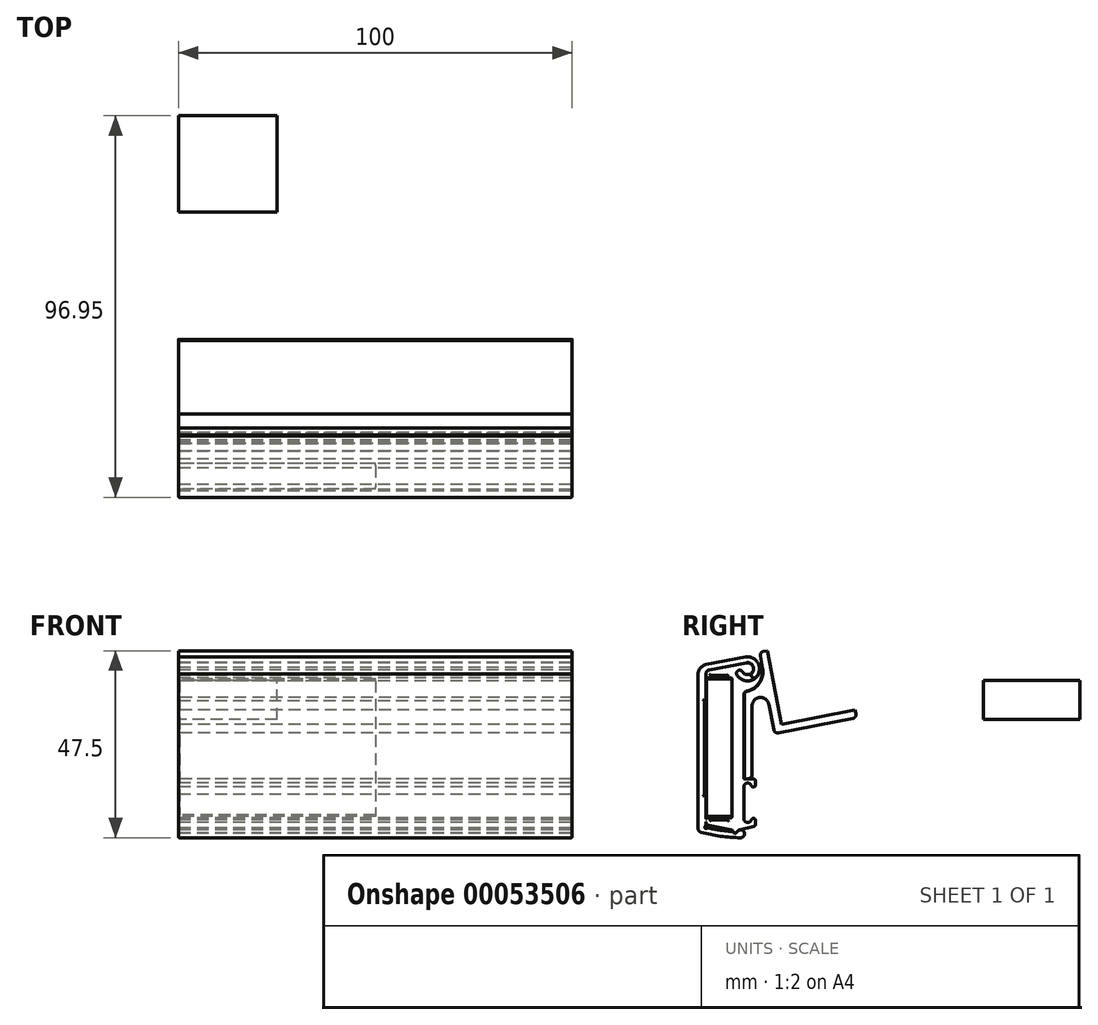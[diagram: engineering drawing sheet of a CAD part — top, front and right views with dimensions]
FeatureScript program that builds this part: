
annotation { "Feature Type Name" : "Feature", "Feature Type Description" : "" }
export const myFeature = defineFeature(function(context is Context, id is Id, definition is map)
    precondition{}
    {
        {
            var Q0;
            Q0=qCreatedBy(makeId("Right.planeOp"),FACE);
            var sketch = newSketch(context, id + "F0", { "sketchPlane" : qUnion([Q0])});
            skLineSegment(sketch, "E0.bottom", {"start": v(-0.5, 35) * mm, "end": v(-6, 35) * mm});
            skLineSegment(sketch, "E0.top", {"start": v(-0.5, 0) * mm, "end": v(-6, 0) * mm});
            skLineSegment(sketch, "E0.left", {"start": v(0, 34.5) * mm, "end": v(0, 0.5) * mm});
            skLineSegment(sketch, "E0.right", {"start": v(-6.5, 34.5) * mm, "end": v(-6.5, 0.5) * mm});
            skPoint(sketch, "E1.visualSharp", {"position": v(0, 35) * mm});
            skArc(sketch, "E1.filletArc", {"start": v(0, 34.5) * mm, "mid": v(-0.15, 34.85) * mm, "end": v(-0.5, 35) * mm});
            skPoint(sketch, "E2.visualSharp", {"position": v(-6.5, 35) * mm});
            skArc(sketch, "E2.filletArc", {"start": v(-6, 35) * mm, "mid": v(-6.35, 34.85) * mm, "end": v(-6.5, 34.5) * mm});
            skPoint(sketch, "E3.visualSharp", {"position": v(-6.5, 0) * mm});
            skArc(sketch, "E3.filletArc", {"start": v(-6.5, 0.5) * mm, "mid": v(-6.35, 0.15) * mm, "end": v(-6, 0) * mm});
            skPoint(sketch, "E4.visualSharp", {"position": v(0, 0) * mm});
            skArc(sketch, "E4.filletArc", {"start": v(-0.5, 0) * mm, "mid": v(-0.15, 0.15) * mm, "end": v(0, 0.5) * mm});
            skLineSegment(sketch, "E5", {"start": v(-6.5, 17.5) * mm, "end": v(0, 17.5) * mm, "construction": true});
            skLineSegment(sketch, "E6.rect.bottom", {"start": v(-3.25, 35.5) * mm, "end": v(-3.25, 35.5) * mm});
            skLineSegment(sketch, "E6.rect.top", {"start": v(-2.25, 34.5) * mm, "end": v(-4.25, 34.5) * mm, "construction": true});
            skLineSegment(sketch, "E6.rect.left", {"start": v(-2.25, 34.5) * mm, "end": v(-2.25, 34.5) * mm});
            skLineSegment(sketch, "E6.rect.right", {"start": v(-4.25, 34.5) * mm, "end": v(-4.25, 34.5) * mm});
            skPoint(sketch, "E6.rect.middle", {"position": v(-3.25, 35) * mm});
            skPoint(sketch, "E7.visualSharp", {"position": v(-4.25, 35.5) * mm});
            skArc(sketch, "E7.filletArc", {"start": v(-3.25, 35.5) * mm, "mid": v(-3.96, 35.2) * mm, "end": v(-4.25, 34.5) * mm, "construction": true});
            skPoint(sketch, "E8.visualSharp", {"position": v(-2.25, 35.5) * mm});
            skArc(sketch, "E8.filletArc", {"start": v(-2.25, 34.5) * mm, "mid": v(-2.54, 35.2) * mm, "end": v(-3.25, 35.5) * mm, "construction": true});
            skPoint(sketch, "E9.MirrorP", {"position": v(-3.25, 0) * mm});
            skPoint(sketch, "E10.MirrorP", {"position": v(-2.25, -0.5) * mm});
            skArc(sketch, "E11.MirrorCS", {"start": v(-2.25, 0.5) * mm, "mid": v(-2.54, -0.2) * mm, "end": v(-3.25, -0.5) * mm, "construction": true});
            skPoint(sketch, "E12.MirrorP", {"position": v(-4.25, -0.5) * mm});
            skLineSegment(sketch, "E13.MirrorCS", {"start": v(-3.25, -0.5) * mm, "end": v(-3.25, -0.5) * mm});
            skArc(sketch, "E14.MirrorCS", {"start": v(-3.25, -0.5) * mm, "mid": v(-3.96, -0.2) * mm, "end": v(-4.25, 0.5) * mm, "construction": true});
            skLineSegment(sketch, "E15.MirrorCS", {"start": v(-4.25, 0.5) * mm, "end": v(-4.25, 0.5) * mm});
            skLineSegment(sketch, "E16.MirrorCS", {"start": v(-2.25, 0.5) * mm, "end": v(-4.25, 0.5) * mm, "construction": true});
            skLineSegment(sketch, "E17.MirrorCS", {"start": v(-2.25, 0.5) * mm, "end": v(-2.25, 0.5) * mm});
            skLineSegment(sketch, "E18.rect.bottom", {"start": v(-6, 29.4) * mm, "end": v(-6.5, 29.4) * mm});
            skLineSegment(sketch, "E18.rect.top", {"start": v(-6, 5.6) * mm, "end": v(-6.5, 5.6) * mm});
            skLineSegment(sketch, "E18.rect.left", {"start": v(-6, 29.4) * mm, "end": v(-6, 5.6) * mm, "construction": true});
            skPoint(sketch, "E18.rect.middle", {"position": v(-6.5, 17.5) * mm});
            skPoint(sketch, "E18.rect.right.end.orphan", {"position": v(-7, 5.6) * mm});
            skPoint(sketch, "E18.rect.right.start.orphan", {"position": v(-7, 29.4) * mm});
            skSolve(sketch);
        }
        {
            var Q0;
            Q0=qCreatedBy(makeId("Right.planeOp"),FACE);
            var sketch = newSketch(context, id + "F1", { "sketchPlane" : qUnion([Q0])});
            skLineSegment(sketch, "E19", {"start": v(-6.3, 35.3) * mm, "end": v(-5.65, 35.3) * mm});
            skLineSegment(sketch, "E20", {"start": v(0, 35) * mm, "end": v(0, 0) * mm});
            skLineSegment(sketch, "E21", {"start": v(-0.3, -0.3) * mm, "end": v(-0.85, -0.3) * mm});
            skLineSegment(sketch, "E22", {"start": v(-12.05, -2.3) * mm, "end": v(-5.6, -2.3) * mm, "construction": true});
            skLineSegment(sketch, "E23", {"start": v(-5.35, 35.6) * mm, "end": v(-5.35, 35.85) * mm});
            skLineSegment(sketch, "E24", {"start": v(-5.35, 35.85) * mm, "end": v(-1.15, 35.85) * mm});
            skLineSegment(sketch, "E25", {"start": v(-1.15, 35.85) * mm, "end": v(-1.15, 35.6) * mm});
            skLineSegment(sketch, "E26.trimOffspring", {"start": v(-0.85, 35.3) * mm, "end": v(-0.3, 35.3) * mm});
            skLineSegment(sketch, "E27.MirrorCS", {"start": v(-1.15, -0.85) * mm, "end": v(-1.15, -0.6) * mm});
            skLineSegment(sketch, "E28.MirrorCS", {"start": v(-5.35, -0.6) * mm, "end": v(-5.35, -0.85) * mm});
            skLineSegment(sketch, "E29.MirrorCS", {"start": v(-5.35, -0.85) * mm, "end": v(-1.15, -0.85) * mm});
            skLineSegment(sketch, "E30.trimOffspring", {"start": v(-5.65, -0.3) * mm, "end": v(-6.3, -0.3) * mm});
            skPoint(sketch, "E31.visualSharp", {"position": v(-6, 35.3) * mm});
            skArc(sketch, "E31.filletArc", {"start": v(-6.6, 35.6) * mm, "mid": v(-6.51, 35.39) * mm, "end": v(-6.3, 35.3) * mm});
            skPoint(sketch, "E32.visualSharp", {"position": v(-5.35, 35.3) * mm});
            skArc(sketch, "E32.filletArc", {"start": v(-5.65, 35.3) * mm, "mid": v(-5.44, 35.39) * mm, "end": v(-5.35, 35.6) * mm});
            skPoint(sketch, "E33.visualSharp", {"position": v(0, 35.3) * mm});
            skArc(sketch, "E33.filletArc", {"start": v(0, 35) * mm, "mid": v(-0.09, 35.21) * mm, "end": v(-0.3, 35.3) * mm});
            skPoint(sketch, "E34.visualSharp", {"position": v(-1.15, 35.3) * mm});
            skArc(sketch, "E34.filletArc", {"start": v(-1.15, 35.6) * mm, "mid": v(-1.06, 35.39) * mm, "end": v(-0.85, 35.3) * mm});
            skPoint(sketch, "E35.visualSharp", {"position": v(-6, -0.3) * mm});
            skArc(sketch, "E35.filletArc", {"start": v(-6.3, -0.3) * mm, "mid": v(-6.51, -0.39) * mm, "end": v(-6.6, -0.6) * mm});
            skPoint(sketch, "E36.visualSharp", {"position": v(-5.35, -0.3) * mm});
            skArc(sketch, "E36.filletArc", {"start": v(-5.35, -0.6) * mm, "mid": v(-5.44, -0.39) * mm, "end": v(-5.65, -0.3) * mm});
            skPoint(sketch, "E37.visualSharp", {"position": v(-1.15, -0.3) * mm});
            skArc(sketch, "E37.filletArc", {"start": v(-0.85, -0.3) * mm, "mid": v(-1.06, -0.39) * mm, "end": v(-1.15, -0.6) * mm});
            skPoint(sketch, "E38.visualSharp", {"position": v(0, -0.3) * mm});
            skArc(sketch, "E38.filletArc", {"start": v(-0.3, -0.3) * mm, "mid": v(-0.09, -0.21) * mm, "end": v(0, 0) * mm});
            skPoint(sketch, "E39.visualSharp", {"position": v(1.45, 37.5) * mm});
            skPoint(sketch, "E40.visualSharp", {"position": v(-6, 37.5) * mm});
            skPoint(sketch, "E41.visualSharp", {"position": v(-6, -2.3) * mm});
            skArc(sketch, "E41.filletArc", {"start": v(-6.6, -1.3) * mm, "mid": v(-6.37, -1.94) * mm, "end": v(-5.79, -2.28) * mm});
            skArc(sketch, "E42", {"start": v(4.02, -3.35) * mm, "mid": v(-6.17, -2.3) * mm, "end": v(-15.75, 1.34) * mm, "construction": true});
            skLineSegment(sketch, "E43", {"start": v(-5.79, -2.28) * mm, "end": v(-0.09, -3.38) * mm});
            skArc(sketch, "E44", {"start": v(0.23, -3.7) * mm, "mid": v(0.7, -4.17) * mm, "end": v(1.31, -3.87) * mm});
            skPoint(sketch, "E45.visualSharp", {"position": v(0.24, -3.44) * mm});
            skArc(sketch, "E45.filletArc", {"start": v(0.23, -3.7) * mm, "mid": v(0.12, -3.49) * mm, "end": v(-0.09, -3.38) * mm});
            skPoint(sketch, "E46.visualSharp", {"position": v(1.32, -3.33) * mm});
            skPoint(sketch, "E47.visualSharp", {"position": v(-12.05, -2.3) * mm});
            skLineSegment(sketch, "E48", {"start": v(5.5, 9.53) * mm, "end": v(3.23, 9.53) * mm});
            skPoint(sketch, "E49.visualSharp", {"position": v(7.02, 9.53) * mm});
            skLineSegment(sketch, "E50.trimOffspring", {"start": v(3.03, 9.73) * mm, "end": v(3.03, 30.94) * mm});
            skPoint(sketch, "E51.visualSharp", {"position": v(7.02, 6.35) * mm});
            skPoint(sketch, "E52.visualSharp", {"position": v(3.03, 9.53) * mm});
            skArc(sketch, "E52.filletArc", {"start": v(3.03, 9.73) * mm, "mid": v(3.1, 9.6) * mm, "end": v(3.23, 9.53) * mm});
            skLineSegment(sketch, "E53", {"start": v(6, 9.03) * mm, "end": v(6, 8.03) * mm});
            skLineSegment(sketch, "E54", {"start": v(5.5, 7.53) * mm, "end": v(5.41, 7.53) * mm});
            skLineSegment(sketch, "E55", {"start": v(3, 7.53) * mm, "end": v(3, -0.47) * mm});
            skLineSegment(sketch, "E56", {"start": v(5.41, -0.47) * mm, "end": v(5.5, -0.47) * mm});
            skArc(sketch, "E57", {"start": v(3, 7.53) * mm, "mid": v(3.83, 8.51) * mm, "end": v(4.94, 7.86) * mm});
            skArc(sketch, "E58", {"start": v(3, -0.47) * mm, "mid": v(3.83, -1.46) * mm, "end": v(4.94, -0.8) * mm});
            skPoint(sketch, "E59.visualSharp", {"position": v(5, 7.53) * mm});
            skArc(sketch, "E59.filletArc", {"start": v(4.94, 7.86) * mm, "mid": v(5.13, 7.62) * mm, "end": v(5.41, 7.53) * mm});
            skPoint(sketch, "E60.newPointA", {"position": v(7, 7.53) * mm});
            skArc(sketch, "E60.filletArc", {"start": v(5.5, 7.53) * mm, "mid": v(5.85, 7.67) * mm, "end": v(6, 8.03) * mm});
            skPoint(sketch, "E61.visualSharp", {"position": v(5, -0.47) * mm});
            skArc(sketch, "E61.filletArc", {"start": v(5.41, -0.47) * mm, "mid": v(5.13, -0.57) * mm, "end": v(4.94, -0.8) * mm});
            skLineSegment(sketch, "E62", {"start": v(6, -0.97) * mm, "end": v(6, -1.98) * mm});
            skPoint(sketch, "E63.visualSharp", {"position": v(6, -0.47) * mm});
            skArc(sketch, "E63.filletArc", {"start": v(6, -0.97) * mm, "mid": v(5.85, -0.62) * mm, "end": v(5.5, -0.47) * mm});
            skPoint(sketch, "E64.visualSharp", {"position": v(6, 9.53) * mm});
            skArc(sketch, "E64.filletArc", {"start": v(6, 9.03) * mm, "mid": v(5.85, 9.39) * mm, "end": v(5.5, 9.53) * mm});
            skLineSegment(sketch, "E65.bottom", {"start": v(-5.35, 35.85) * mm, "end": v(-1.15, 35.85) * mm, "construction": true});
            skLineSegment(sketch, "E65.top", {"start": v(-5.35, 35.5) * mm, "end": v(-1.15, 35.5) * mm, "construction": true});
            skLineSegment(sketch, "E65.left", {"start": v(-5.35, 35.85) * mm, "end": v(-5.35, 35.5) * mm, "construction": true});
            skLineSegment(sketch, "E65.right", {"start": v(-1.15, 35.85) * mm, "end": v(-1.15, 35.5) * mm, "construction": true});
            skLineSegment(sketch, "E66", {"start": v(-3.25, 35.85) * mm, "end": v(-3.25, 34.98) * mm, "construction": true});
            skPoint(sketch, "E66.endSnap0", {"position": v(-3.25, 35.85) * mm});
            skLineSegment(sketch, "E67", {"start": v(-6.6, -0.6) * mm, "end": v(-6.6, -1.3) * mm});
            skPoint(sketch, "E68.startSnap0", {"position": v(5.5, 34.89) * mm});
            skLineSegment(sketch, "E69", {"start": v(3.03, 31.44) * mm, "end": v(3.03, 35.7) * mm, "construction": true});
            skPoint(sketch, "E70.visualSharp", {"position": v(3.03, 30.76) * mm});
            skArc(sketch, "E70.filletArc", {"start": v(4.46, 30.97) * mm, "mid": v(3.43, 30.25) * mm, "end": v(3.03, 29.06) * mm, "construction": true});
            skArc(sketch, "E71", {"start": v(1.31, -3.87) * mm, "mid": v(1.58, -3.56) * mm, "end": v(1.96, -3.38) * mm});
            skLineSegment(sketch, "E72", {"start": v(1.96, -3.38) * mm, "end": v(5.62, -2.47) * mm});
            skPoint(sketch, "E73.visualSharp", {"position": v(6, -2.37) * mm});
            skArc(sketch, "E73.filletArc", {"start": v(5.62, -2.47) * mm, "mid": v(5.9, -2.29) * mm, "end": v(6, -1.98) * mm});
            skArc(sketch, "E74", {"start": v(3.69, 39.04) * mm, "mid": v(5.32, 36.94) * mm, "end": v(2.66, 36.81) * mm});
            skLineSegment(sketch, "E75", {"start": v(-5.73, 37.3) * mm, "end": v(3.69, 39.04) * mm});
            skArc(sketch, "E76", {"start": v(-5.73, 37.3) * mm, "mid": v(-6.35, 36.93) * mm, "end": v(-6.6, 36.25) * mm});
            skLineSegment(sketch, "E77", {"start": v(-6.6, 35.6) * mm, "end": v(-6.6, 36.25) * mm});
            skLineSegment(sketch, "E78", {"start": v(3.96, 37.56) * mm, "end": v(2.66, 36.81) * mm, "construction": true});
            skArc(sketch, "E79", {"start": v(1.28, 36.01) * mm, "mid": v(4.76, 34.57) * mm, "end": v(7.06, 37.56) * mm});
            skArc(sketch, "E80", {"start": v(7.06, 37.56) * mm, "mid": v(7.37, 37.9) * mm, "end": v(7.72, 37.62) * mm});
            skArc(sketch, "E81", {"start": v(7.72, 37.62) * mm, "mid": v(6.91, 33.99) * mm, "end": v(3.83, 31.92) * mm});
            skArc(sketch, "E82", {"start": v(2.66, 36.81) * mm, "mid": v(1.57, 37.1) * mm, "end": v(1.28, 36.01) * mm});
            skPoint(sketch, "E83.visualSharp", {"position": v(3.03, 31.82) * mm});
            skArc(sketch, "E83.filletArc", {"start": v(3.83, 31.92) * mm, "mid": v(3.26, 31.57) * mm, "end": v(3.03, 30.94) * mm});
            skLineSegment(sketch, "E84", {"start": v(3.96, 37.56) * mm, "end": v(7.4, 37.56) * mm, "construction": true});
            skLineSegment(sketch, "E85", {"start": v(3.96, 37.56) * mm, "end": v(3.96, 34.96) * mm, "construction": true});
            skSolve(sketch);
        }
        {
            var Q0;
            Q0=qCreatedBy(makeId("Right.planeOp"),FACE);
            var sketch = newSketch(context, id + "F2", { "sketchPlane" : qUnion([Q0])});
            skLineSegment(sketch, "E86.2", {"start": v(-5.6, 37.3) * mm, "end": v(-5.6, 37.3) * mm});
            skArc(sketch, "E87.1", {"start": v(-6.58, 38.62) * mm, "mid": v(-7.99, 37.8) * mm, "end": v(-8.6, 36.3) * mm});
            skLineSegment(sketch, "E88", {"start": v(-8.6, 36.3) * mm, "end": v(-8.6, -3) * mm});
            skPoint(sketch, "E89.visualSharp", {"position": v(-6.03, 35.1) * mm});
            skArc(sketch, "E90", {"start": v(-5.8, -2.92) * mm, "mid": v(-2.9, -3.45) * mm, "end": v(0.01, -3.77) * mm});
            skArc(sketch, "E91.0", {"start": v(-7.86, -3.96) * mm, "mid": v(-2.88, -4.97) * mm, "end": v(2.18, -5.37) * mm});
            skPoint(sketch, "E92.trimOffspring.end.orphan", {"position": v(-7.6, -5.55) * mm});
            skPoint(sketch, "E93.orphan", {"position": v(-8.6, -5.55) * mm});
            skPoint(sketch, "E94.visualSharp", {"position": v(-8.6, -3.75) * mm});
            skArc(sketch, "E94.filletArc", {"start": v(-8.6, -3) * mm, "mid": v(-8.4, -3.6) * mm, "end": v(-7.86, -3.96) * mm});
            skPoint(sketch, "E95.visualSharp", {"position": v(12.44, -2.73) * mm});
            skLineSegment(sketch, "E96.0", {"start": v(-6.6, 36.25) * mm, "end": v(-6.6, 29.4) * mm});
            skArc(sketch, "E97", {"start": v(-6.83, -2.54) * mm, "mid": v(-6.83, -2.92) * mm, "end": v(-6.46, -3) * mm});
            skPoint(sketch, "E98.visualSharp", {"position": v(-6.6, -2.43) * mm});
            skArc(sketch, "E98.filletArc", {"start": v(-6.83, -2.54) * mm, "mid": v(-6.66, -2.24) * mm, "end": v(-6.6, -1.9) * mm});
            skPoint(sketch, "E99.visualSharp", {"position": v(-6.3, -2.8) * mm});
            skArc(sketch, "E99.filletArc", {"start": v(-5.8, -2.92) * mm, "mid": v(-6.14, -2.9) * mm, "end": v(-6.46, -3) * mm});
            skPoint(sketch, "E100.visualSharp", {"position": v(0.78, -3.82) * mm});
            skLineSegment(sketch, "E101", {"start": v(-6.6, 29.4) * mm, "end": v(-7, 29.4) * mm});
            skLineSegment(sketch, "E102", {"start": v(-6.6, 5.6) * mm, "end": v(-7, 5.6) * mm});
            skLineSegment(sketch, "E103", {"start": v(-7, 5.6) * mm, "end": v(-7, 29.4) * mm});
            skLineSegment(sketch, "E104.trimOffspring", {"start": v(-6.6, 5.6) * mm, "end": v(-6.6, -1.9) * mm});
            skArc(sketch, "E105", {"start": v(1.33, -3.88) * mm, "mid": v(3.07, -3.87) * mm, "end": v(2.18, -5.37) * mm});
            skArc(sketch, "E106", {"start": v(0.31, -3.94) * mm, "mid": v(0.83, -4.2) * mm, "end": v(1.33, -3.88) * mm});
            skPoint(sketch, "E107.visualSharp", {"position": v(0.23, -3.78) * mm});
            skArc(sketch, "E107.filletArc", {"start": v(0.31, -3.94) * mm, "mid": v(0.18, -3.82) * mm, "end": v(0.01, -3.77) * mm});
            skLineSegment(sketch, "E108", {"start": v(-6.58, 38.62) * mm, "end": v(3.39, 40.54) * mm});
            skLineSegment(sketch, "E109", {"start": v(-5.74, 37.3) * mm, "end": v(3.66, 39.1) * mm});
            skArc(sketch, "E110", {"start": v(3.39, 40.54) * mm, "mid": v(6.63, 39) * mm, "end": v(6.14, 35.46) * mm});
            skArc(sketch, "E111", {"start": v(3.66, 39.1) * mm, "mid": v(5.34, 38.31) * mm, "end": v(5.09, 36.47) * mm});
            skLineSegment(sketch, "E112", {"start": v(3.96, 37.56) * mm, "end": v(11, 38.92) * mm, "construction": true});
            skLineSegment(sketch, "E113", {"start": v(3.96, 37.56) * mm, "end": v(6.14, 35.46) * mm, "construction": true});
            skArc(sketch, "E114", {"start": v(5.09, 36.47) * mm, "mid": v(5.1, 35.44) * mm, "end": v(6.14, 35.46) * mm});
            skArc(sketch, "E115", {"start": v(-6.6, 36.25) * mm, "mid": v(-6.36, 36.93) * mm, "end": v(-5.74, 37.3) * mm});
            skSolve(sketch);
        }
        {
            var Q0;
            Q0=qCreatedBy(makeId("Right.planeOp"),FACE);
            var sketch = newSketch(context, id + "F3", { "sketchPlane" : qUnion([Q0])});
            skLineSegment(sketch, "E116.2", {"start": v(3.13, 9.63) * mm, "end": v(3.13, 30.94) * mm});
            skLineSegment(sketch, "E117", {"start": v(3.13, 9.63) * mm, "end": v(4.13, 9.63) * mm});
            skLineSegment(sketch, "E118", {"start": v(5.13, 10.63) * mm, "end": v(5.13, 28.17) * mm});
            skPoint(sketch, "E119.visualSharp", {"position": v(7, 40) * mm});
            skArc(sketch, "E119.filletArc", {"start": v(8.01, 41.94) * mm, "mid": v(7.37, 41.52) * mm, "end": v(7.22, 40.77) * mm});
            skPoint(sketch, "E120.visualSharp", {"position": v(11.58, -2.41) * mm});
            skLineSegment(sketch, "E121", {"start": v(8.01, 41.94) * mm, "end": v(9, 42.13) * mm});
            skLineSegment(sketch, "E122", {"start": v(7.8, 37.78) * mm, "end": v(7.22, 40.77) * mm});
            skLineSegment(sketch, "E123", {"start": v(9, 42.13) * mm, "end": v(12.6, 23.47) * mm});
            skLineSegment(sketch, "E124", {"start": v(12.6, 23.47) * mm, "end": v(31.25, 27.07) * mm});
            skLineSegment(sketch, "E125", {"start": v(31.25, 27.07) * mm, "end": v(31.48, 26.16) * mm});
            skLineSegment(sketch, "E126", {"start": v(30.7, 24.93) * mm, "end": v(11.79, 21.28) * mm});
            skLineSegment(sketch, "E127", {"start": v(10.62, 22.07) * mm, "end": v(9.36, 28.57) * mm});
            skArc(sketch, "E128", {"start": v(9.36, 28.57) * mm, "mid": v(7.06, 30.3) * mm, "end": v(5.13, 28.17) * mm});
            skArc(sketch, "E129.0", {"start": v(3.85, 31.82) * mm, "mid": v(3.33, 31.5) * mm, "end": v(3.13, 30.94) * mm});
            skArc(sketch, "E129.1", {"start": v(7.8, 37.78) * mm, "mid": v(7.04, 34) * mm, "end": v(3.85, 31.82) * mm});
            skPoint(sketch, "E130.visualSharp", {"position": v(10.8, 21.1) * mm});
            skArc(sketch, "E130.filletArc", {"start": v(10.62, 22.07) * mm, "mid": v(11.04, 21.44) * mm, "end": v(11.79, 21.28) * mm});
            skPoint(sketch, "E131.visualSharp", {"position": v(31.75, 25.13) * mm});
            skArc(sketch, "E131.filletArc", {"start": v(30.7, 24.93) * mm, "mid": v(31.36, 25.38) * mm, "end": v(31.48, 26.16) * mm});
            skPoint(sketch, "E132.visualSharp", {"position": v(5.13, 9.63) * mm});
            skArc(sketch, "E132.filletArc", {"start": v(4.13, 9.63) * mm, "mid": v(4.84, 9.93) * mm, "end": v(5.13, 10.63) * mm});
            skSolve(sketch);
        }
        {
            var Q0;
            Q0=qSketchRegion(id+"F1",true);
            extrude(context, id + "F4", {"entities" : qUnion([Q0]), "depth" : 100 * mm});
        }
        {
            var Q0;
            Q0=qSketchRegion(id+"F2",true);
            extrude(context, id + "F5", {"entities" : qUnion([Q0]), "depth" : 100 * mm});
        }
        {
            var Q0;
            Q0=makeQuery(id+"F5.opExtrude","CAP_FACE",FACE,{"disambiguationData":[OSD([sQuery(id+"F2.wireOp",EDGE,"E86.2"),sQuery(id+"F2.wireOp",EDGE,"E86.3"),sQuery(id+"F2.wireOp",EDGE,"E87.1"),sQuery(id+"F2.wireOp",EDGE,"E88"),sQuery(id+"F2.wireOp",EDGE,"E90"),sQuery(id+"F2.wireOp",EDGE,"E91.0"),sQuery(id+"F2.wireOp",EDGE,"E94.filletArc"),sQuery(id+"F2.wireOp",EDGE,"E96.0"),sQuery(id+"F2.wireOp",EDGE,"E97"),sQuery(id+"F2.wireOp",EDGE,"E98.filletArc"),sQuery(id+"F2.wireOp",EDGE,"E99.filletArc"),sQuery(id+"F2.wireOp",EDGE,"E101"),sQuery(id+"F2.wireOp",EDGE,"E102"),sQuery(id+"F2.wireOp",EDGE,"E103"),sQuery(id+"F2.wireOp",EDGE,"E104.trimOffspring"),sQuery(id+"F2.wireOp",EDGE,"a8f8e689-5e16-47e5-8057-b0ad275942a9"),sQuery(id+"F2.wireOp",EDGE,"E105"),sQuery(id+"F2.wireOp",EDGE,"E106"),sQuery(id+"F2.wireOp",EDGE,"E107.filletArc"),sQuery(id+"F2.wireOp",EDGE,"12610329-de8c-4fad-bd06-cedb4965ef3b.0"),sQuery(id+"F2.wireOp",EDGE,"fd023df9-4820-42a8-a1c4-7477257e8a0a.0"),sQuery(id+"F2.wireOp",EDGE,"7f343079-0b22-43a6-ac4e-2e25a93e7ffd")])],"isStart":false});
            var Q1;
            Q1=makeQuery(id+"F5.opExtrude","CAP_FACE",FACE,{"disambiguationData":[OSD([sQuery(id+"F2.wireOp",EDGE,"E86.2"),sQuery(id+"F2.wireOp",EDGE,"E86.3"),sQuery(id+"F2.wireOp",EDGE,"E87.1"),sQuery(id+"F2.wireOp",EDGE,"E88"),sQuery(id+"F2.wireOp",EDGE,"E90"),sQuery(id+"F2.wireOp",EDGE,"E91.0"),sQuery(id+"F2.wireOp",EDGE,"E94.filletArc"),sQuery(id+"F2.wireOp",EDGE,"E96.0"),sQuery(id+"F2.wireOp",EDGE,"E97"),sQuery(id+"F2.wireOp",EDGE,"E98.filletArc"),sQuery(id+"F2.wireOp",EDGE,"E99.filletArc"),sQuery(id+"F2.wireOp",EDGE,"E101"),sQuery(id+"F2.wireOp",EDGE,"E102"),sQuery(id+"F2.wireOp",EDGE,"E103"),sQuery(id+"F2.wireOp",EDGE,"E104.trimOffspring"),sQuery(id+"F2.wireOp",EDGE,"a8f8e689-5e16-47e5-8057-b0ad275942a9"),sQuery(id+"F2.wireOp",EDGE,"E105"),sQuery(id+"F2.wireOp",EDGE,"E106"),sQuery(id+"F2.wireOp",EDGE,"E107.filletArc"),sQuery(id+"F2.wireOp",EDGE,"12610329-de8c-4fad-bd06-cedb4965ef3b.0"),sQuery(id+"F2.wireOp",EDGE,"fd023df9-4820-42a8-a1c4-7477257e8a0a.0"),sQuery(id+"F2.wireOp",EDGE,"7f343079-0b22-43a6-ac4e-2e25a93e7ffd")])],"isStart":true});
            fillet(context, id + "F6", {"entities" : qUnion([Q0, Q1]), "radius" : .3 * mm, "tangentPropagation" : true, "allowEdgeOverflow" : false});
        }
        {
            var Q0;
            Q0=makeQuery(id+"F4.opExtrude","CAP_FACE",FACE,{"disambiguationData":[OSD([sQuery(id+"F1.wireOp",EDGE,"E19"),sQuery(id+"F1.wireOp",EDGE,"E20"),sQuery(id+"F1.wireOp",EDGE,"E21"),sQuery(id+"F1.wireOp",EDGE,"E23"),sQuery(id+"F1.wireOp",EDGE,"E24"),sQuery(id+"F1.wireOp",EDGE,"E25"),sQuery(id+"F1.wireOp",EDGE,"E26.trimOffspring"),sQuery(id+"F1.wireOp",EDGE,"E27.MirrorCS"),sQuery(id+"F1.wireOp",EDGE,"E28.MirrorCS"),sQuery(id+"F1.wireOp",EDGE,"E29.MirrorCS"),sQuery(id+"F1.wireOp",EDGE,"E30.trimOffspring"),sQuery(id+"F1.wireOp",EDGE,"E31.filletArc"),sQuery(id+"F1.wireOp",EDGE,"E32.filletArc"),sQuery(id+"F1.wireOp",EDGE,"E33.filletArc"),sQuery(id+"F1.wireOp",EDGE,"E34.filletArc"),sQuery(id+"F1.wireOp",EDGE,"E35.filletArc"),sQuery(id+"F1.wireOp",EDGE,"E36.filletArc"),sQuery(id+"F1.wireOp",EDGE,"E37.filletArc"),sQuery(id+"F1.wireOp",EDGE,"E38.filletArc"),sQuery(id+"F1.wireOp",EDGE,"E40.filletArc"),sQuery(id+"F1.wireOp",EDGE,"E41.filletArc"),sQuery(id+"F1.wireOp",EDGE,"E43"),sQuery(id+"F1.wireOp",EDGE,"E44"),sQuery(id+"F1.wireOp",EDGE,"E45.filletArc"),sQuery(id+"F1.wireOp",EDGE,"E48"),sQuery(id+"F1.wireOp",EDGE,"E50.trimOffspring"),sQuery(id+"F1.wireOp",EDGE,"E52.filletArc"),sQuery(id+"F1.wireOp",EDGE,"E53"),sQuery(id+"F1.wireOp",EDGE,"E54"),sQuery(id+"F1.wireOp",EDGE,"E55"),sQuery(id+"F1.wireOp",EDGE,"E56"),sQuery(id+"F1.wireOp",EDGE,"E57"),sQuery(id+"F1.wireOp",EDGE,"E58"),sQuery(id+"F1.wireOp",EDGE,"E59.filletArc"),sQuery(id+"F1.wireOp",EDGE,"E60.filletArc"),sQuery(id+"F1.wireOp",EDGE,"E61.filletArc"),sQuery(id+"F1.wireOp",EDGE,"E62"),sQuery(id+"F1.wireOp",EDGE,"E63.filletArc"),sQuery(id+"F1.wireOp",EDGE,"E64.filletArc"),sQuery(id+"F1.wireOp",EDGE,"9542a1ec-a0dd-46c9-bb78-918edde2ff07"),sQuery(id+"F1.wireOp",EDGE,"98c17557-ba8b-4a89-b03a-64bb9ddbf5dd"),sQuery(id+"F1.wireOp",EDGE,"E67"),sQuery(id+"F1.wireOp",EDGE,"bf3c36d9-637c-44d3-a7fd-f6e3cdd292ba"),sQuery(id+"F1.wireOp",EDGE,"c5bfcd06-bca6-4be6-b2b0-0e9924831b46"),sQuery(id+"F1.wireOp",EDGE,"5fbb8a50-3f5f-4460-b2ad-e5d3e9a667ab"),sQuery(id+"F1.wireOp",EDGE,"fa309500-8770-4dd0-bda2-21b0fca20fbb"),sQuery(id+"F1.wireOp",EDGE,"0d5ed8aa-ec24-4a5e-be27-1346574a6d7d"),sQuery(id+"F1.wireOp",EDGE,"E70.filletArc"),sQuery(id+"F1.wireOp",EDGE,"E71"),sQuery(id+"F1.wireOp",EDGE,"E72"),sQuery(id+"F1.wireOp",EDGE,"E73.filletArc")])],"isStart":false});
            var Q1;
            Q1=makeQuery(id+"F4.opExtrude","CAP_FACE",FACE,{"disambiguationData":[OSD([sQuery(id+"F1.wireOp",EDGE,"E19"),sQuery(id+"F1.wireOp",EDGE,"E20"),sQuery(id+"F1.wireOp",EDGE,"E21"),sQuery(id+"F1.wireOp",EDGE,"E23"),sQuery(id+"F1.wireOp",EDGE,"E24"),sQuery(id+"F1.wireOp",EDGE,"E25"),sQuery(id+"F1.wireOp",EDGE,"E26.trimOffspring"),sQuery(id+"F1.wireOp",EDGE,"E27.MirrorCS"),sQuery(id+"F1.wireOp",EDGE,"E28.MirrorCS"),sQuery(id+"F1.wireOp",EDGE,"E29.MirrorCS"),sQuery(id+"F1.wireOp",EDGE,"E30.trimOffspring"),sQuery(id+"F1.wireOp",EDGE,"E31.filletArc"),sQuery(id+"F1.wireOp",EDGE,"E32.filletArc"),sQuery(id+"F1.wireOp",EDGE,"E33.filletArc"),sQuery(id+"F1.wireOp",EDGE,"E34.filletArc"),sQuery(id+"F1.wireOp",EDGE,"E35.filletArc"),sQuery(id+"F1.wireOp",EDGE,"E36.filletArc"),sQuery(id+"F1.wireOp",EDGE,"E37.filletArc"),sQuery(id+"F1.wireOp",EDGE,"E38.filletArc"),sQuery(id+"F1.wireOp",EDGE,"E40.filletArc"),sQuery(id+"F1.wireOp",EDGE,"E41.filletArc"),sQuery(id+"F1.wireOp",EDGE,"E43"),sQuery(id+"F1.wireOp",EDGE,"E44"),sQuery(id+"F1.wireOp",EDGE,"E45.filletArc"),sQuery(id+"F1.wireOp",EDGE,"E48"),sQuery(id+"F1.wireOp",EDGE,"E50.trimOffspring"),sQuery(id+"F1.wireOp",EDGE,"E52.filletArc"),sQuery(id+"F1.wireOp",EDGE,"E53"),sQuery(id+"F1.wireOp",EDGE,"E54"),sQuery(id+"F1.wireOp",EDGE,"E55"),sQuery(id+"F1.wireOp",EDGE,"E56"),sQuery(id+"F1.wireOp",EDGE,"E57"),sQuery(id+"F1.wireOp",EDGE,"E58"),sQuery(id+"F1.wireOp",EDGE,"E59.filletArc"),sQuery(id+"F1.wireOp",EDGE,"E60.filletArc"),sQuery(id+"F1.wireOp",EDGE,"E61.filletArc"),sQuery(id+"F1.wireOp",EDGE,"E62"),sQuery(id+"F1.wireOp",EDGE,"E63.filletArc"),sQuery(id+"F1.wireOp",EDGE,"E64.filletArc"),sQuery(id+"F1.wireOp",EDGE,"9542a1ec-a0dd-46c9-bb78-918edde2ff07"),sQuery(id+"F1.wireOp",EDGE,"98c17557-ba8b-4a89-b03a-64bb9ddbf5dd"),sQuery(id+"F1.wireOp",EDGE,"E67"),sQuery(id+"F1.wireOp",EDGE,"bf3c36d9-637c-44d3-a7fd-f6e3cdd292ba"),sQuery(id+"F1.wireOp",EDGE,"c5bfcd06-bca6-4be6-b2b0-0e9924831b46"),sQuery(id+"F1.wireOp",EDGE,"5fbb8a50-3f5f-4460-b2ad-e5d3e9a667ab"),sQuery(id+"F1.wireOp",EDGE,"fa309500-8770-4dd0-bda2-21b0fca20fbb"),sQuery(id+"F1.wireOp",EDGE,"0d5ed8aa-ec24-4a5e-be27-1346574a6d7d"),sQuery(id+"F1.wireOp",EDGE,"E70.filletArc"),sQuery(id+"F1.wireOp",EDGE,"E71"),sQuery(id+"F1.wireOp",EDGE,"E72"),sQuery(id+"F1.wireOp",EDGE,"E73.filletArc")])],"isStart":true});
            fillet(context, id + "F7", {"entities" : qUnion([Q0, Q1]), "radius" : .3 * mm, "tangentPropagation" : true, "allowEdgeOverflow" : false});
        }
        {
            var Q0;
            Q0=makeQuery(id+"F3.imprint","IMPRINT",FACE,{"disambiguationData":[TD([[makeQuery(id+"F3.imprint","IMPRINT",EDGE,{"derivedFrom":sQuery(id+"F3.wireOp",EDGE,"E116.2")}),-1.0]])]});
            extrude(context, id + "F8", {"entities" : qUnion([Q0]), "depth" : 100 * mm});
        }
        {
            var Q0;
            Q0=makeQuery(id+"F0.imprint","IMPRINT",FACE,{"disambiguationData":[TD([[makeQuery(id+"F0.imprint","IMPRINT",EDGE,{"derivedFrom":sQuery(id+"F0.wireOp",EDGE,"E0.bottom")}),1.0]])]});
            var sketch = newSketch(context, id + "F9", { "sketchPlane" : qUnion([Q0])});
            skLineSegment(sketch, "E133.bottom", {"start": v(63.84, 24.67) * mm, "end": v(88.35, 24.67) * mm});
            skLineSegment(sketch, "E133.top", {"start": v(63.84, 34.66) * mm, "end": v(88.35, 34.66) * mm});
            skLineSegment(sketch, "E133.left", {"start": v(63.84, 24.67) * mm, "end": v(63.84, 34.66) * mm});
            skLineSegment(sketch, "E133.right", {"start": v(88.35, 24.67) * mm, "end": v(88.35, 34.66) * mm});
            skSolve(sketch);
        }
        {
            var Q0;
            Q0=makeQuery(id+"F9.imprint","IMPRINT",FACE,{"disambiguationData":[TD([[makeQuery(id+"F9.imprint","IMPRINT",EDGE,{"derivedFrom":sQuery(id+"F9.wireOp",EDGE,"E133.bottom")}),1.0]])]});
            extrude(context, id + "F10", {"entities" : qUnion([Q0]), "depth" : 25 * mm});
        }
        {
            var Q0;
            Q0 = qSketchRegion(id + "F0", true);
            extrude(context, id + "F11", {"entities" : qUnion([Q0]), "operationType" : NewBodyOperationType.ADD, "depth" : 50 * mm});
        }
        {
            var Q0;
            Q0 = qSketchRegion(id + "F0", true);
            extrude(context, id + "F12", {"entities" : qUnion([Q0]), "operationType" : NewBodyOperationType.ADD, "depth" : 25 * mm});
        }
    });
